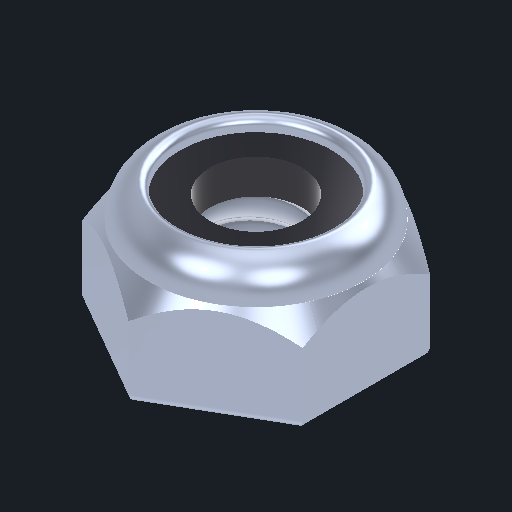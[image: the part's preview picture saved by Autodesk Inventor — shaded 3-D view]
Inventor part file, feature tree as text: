
AUTODESK INVENTOR PART (.ipt)
format: ipt  version: 2024 (Build 280153000, 153)  size: 257,536 bytes
history: native  units: in
note: dims shown in document units (in); Inventor stores cm internally (conversion verified against a paired STEP export)
features: split x2, other x1, imported_body x1, plane x1, thread x1, extrude x1, fillet x1, sketch x1, projected_geometry x1
ambient origin geometry x8: Origin, YZ Plane, XZ Plane, XY Plane, X Axis, Y Axis, Z Axis, Center Point
bodies: Body1 (feature_tree)
feature tree (10):
  parser-record x1  (decoder bookkeeping rows leaked as tree rows — omitted from the tree; the rows remain in map.json)
  imported_body  "Base1"
  plane  "Work Plane1"
  split  "Split1"
  thread  "Thread1"  [1 undecoded]
  split  "Split2"
  extrude  "Extrusion1"  Depth=0.015in TaperAngle=0.0deg
  fillet  "Fillet1"  Radius=0.015in
  sketch  "Sketch1"  dims[d2=-0.05in d5=0.016in d6=0.0in d7=0.015in]
  projected_geometry  "Projected Loop1"
note: 1 required parameter value undecoded (feature->parameter linkage not recoverable at this tier; creation-order binding heuristic only, values carry confidence <= 0.55)
